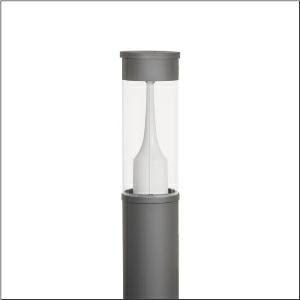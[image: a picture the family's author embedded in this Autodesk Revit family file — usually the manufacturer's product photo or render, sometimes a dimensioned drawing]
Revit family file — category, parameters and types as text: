
# Revit family: city-light_260_iq___st1_2a_5xa5295af14h_a960
name_source: partatom
category: Lighting Fixtures
units: mm (PartAtom-declared; Revit-internal decimal feet)

## family parameters
Cut with Voids When Loaded = No
Host = Face
Light Source = No
Part Type = Normal
Room Calculation Point = No
Round Connector Dimension = Use Diameter
Shared = No

## types (1)
- --- (1 x LED, 1540 lm, 12.9 W, 2200K)
    Apparent Load = 13 VA
    CIE Flux Codes = 22 61 93 96 100
    Color Rendering = 70
    Color Temperature = 2200K
    Default Elevation = 1800 mm
    Description = City-Light 260 iQ, light pillar, Module 540 iQ-SR, primary light control with 3 zone facetted reflector, of plastic, silver coated, highly specular, structured, primary optical cover: cover, of PMMA, transparent, partly coated, light distribution: ST1.2a, primary light characteristic: asymmetric, LED, High Power LED, rated luminous flux: 1.540lm, luminous efficacy: 119lm/W, light colour: 722, colour temperature: 2200K, control gear: ECG iQ, control: presetting dimming logarithmic, Street-Remote, Auto-Match, Temp-Guard, Lumen-Switch, Night-Set, Smart-Wire, Light-Fading, Desk-Remote (wireless, voltage-free reading and setting of iQ features in the workshop via application-optimized NFC function/RFID function), optimised constant luminous flux control (CLO 2.0), with terminal, 6-pole, max. 2.5mm², mains connection: 230..240V, AC, 50/60Hz, start of lifetime: 13W, end of service life: 13W, reduction: 6W, luminaire housing, cylindrical, of extruded aluminium section, coated, Siteco® metallic grey (DB 702S), length: 2.600mm, diameter: 200mm, Module 540 iQ-SR, traffic white (RAL 9016), equipment: standard, protection rating (complete): IP65, insulation class (complete): insulation class II (safety insulation), certification: CE, ENEC, VDE, packaging unit: 1 piece

Light Distribution: ST1.2a
    Height = 500 mm
    Lamp = 1 x LED
    Lamp Light Flux = 1540 lm
    Lamp Power = 12.9 W
    Lamp count = 1
    Length = 200 mm  [stored 0.656168 ft]
    Luminous efficacy = 119 lm/W
    Manufacturer = Siteco
    ModVariant = No
    Model = 5XA5295AF14H
    Mounting Place = Floor
    Mounting Type = Freestanding
    Number of Poles = 1
    OnlyDefault = Yes
    Power Factor = 1
    Product Name = City-Light 260 iQ | ST1.2a
    Product group = light pillar
    ProductGroupID = 1303
    Protection Class = Protection class II
    Protection Degree = IP 65
    RLX_Detail_Level = 1
    RLX_Emergency_Light_Flux = 0 lm
    RLX_Emergency_Type = 0
    RLX_Emergency_Type_DB = No
    RlxData = <blob elided: 61117 chars, md5=15140642>
    Socket = socket
    Standby Power = 0 W
    System Light Flux = 1540 lm
    System Power = 13 W
    Type Comments = factory setting: luminous flux: 100 % | dim-lin: 254 | 516 mA
    Type Image = l_1006918.jpg
    URL = http://relux.com
    VarID = @adj_109411
    Voltage = 0 V
    Weight = 0.00 kg
    Width = 0 mm  [stored 0 ft]

note: [stored X ft] marks values corroborated as IEEE doubles in the binary element streams (Revit-internal decimal feet)

## geometry (parser evidence)
native form markers: Blend x4, Sweep x10
no freeform markers — native parametric forms only
